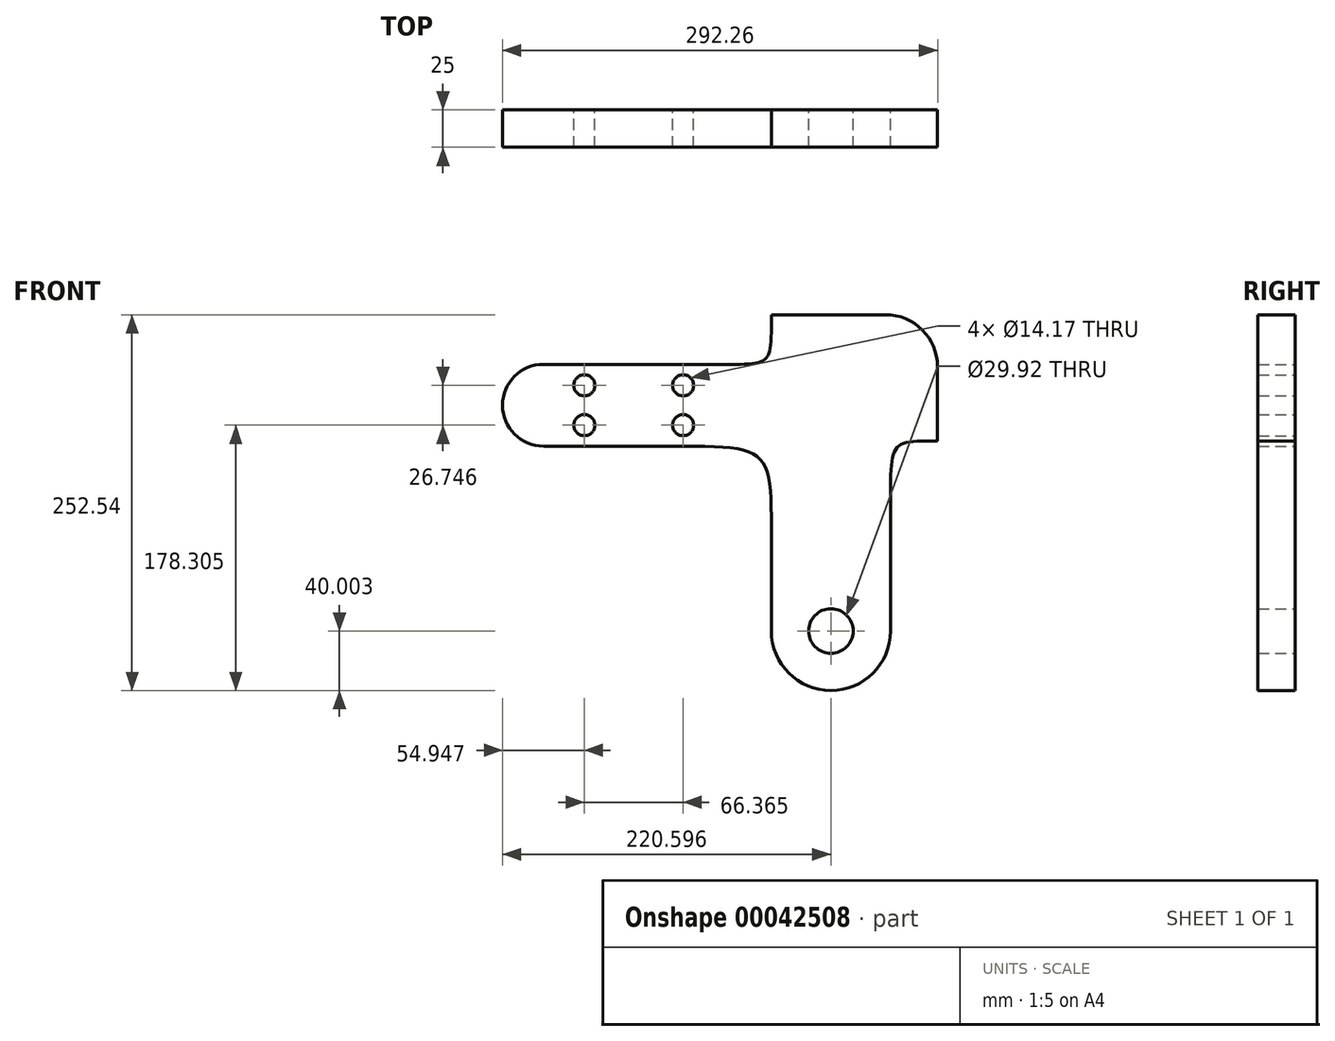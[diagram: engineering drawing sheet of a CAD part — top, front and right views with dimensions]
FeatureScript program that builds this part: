
annotation { "Feature Type Name" : "Feature", "Feature Type Description" : "" }
export const myFeature = defineFeature(function(context is Context, id is Id, definition is map)
    precondition{}
    {
        {
            var Q0;
            Q0=qCreatedBy(makeId("Front.planeOp"),FACE);
            var sketch = newSketch(context, id + "F0", { "sketchPlane" : qUnion([Q0])});
            skLineSegment(sketch, "E0.right", {"start": v(22.5, -51.4) * mm, "end": v(22.5, -113.49) * mm});
            skCircle(sketch, "E1.MirrorC", {"center": v(-36.78, 51.56) * mm, "radius": 7.09 * mm});
            skLineSegment(sketch, "E2.bottom", {"start": v(-9.33, 65.69) * mm, "end": v(-130.6, 65.69) * mm});
            skArc(sketch, "E3", {"start": v(22.5, -113.49) * mm, "mid": v(62.5, -153.49) * mm, "end": v(102.5, -113.49) * mm});
            skFitSpline(sketch, "E4", {"points": [v(22.5, 99.05) * mm, v(-9.33, 65.69) * mm], "startDerivative": vector(0, -103.64) * mm, "endDerivative": vector(-95.5, 0) * mm});
            skFitSpline(sketch, "E5", {"points": [v(134.17, 14.05) * mm, v(102.5, -26.39) * mm], "startDerivative": vector(-94.98, 1.46) * mm, "endDerivative": vector(0, -121.82) * mm});
            skCircle(sketch, "E6", {"center": v(62.5, -113.49) * mm, "radius": 14.96 * mm});
            skLineSegment(sketch, "E7.trimOffspring", {"start": v(22.5, -113.49) * mm, "end": v(22.5, -113.49) * mm});
            skPoint(sketch, "E8.orphan", {"position": v(22.5, 10.69) * mm});
            skLineSegment(sketch, "E9", {"start": v(134.17, 99.05) * mm, "end": v(134.17, 14.05) * mm});
            skLineSegment(sketch, "E10", {"start": v(22.5, 99.05) * mm, "end": v(134.17, 99.05) * mm});
            skLineSegment(sketch, "E0.top", {"start": v(102.5, -113.49) * mm, "end": v(102.5, -113.49) * mm});
            skCircle(sketch, "E11.MirrorC", {"center": v(-36.78, 24.82) * mm, "radius": 7.09 * mm});
            skLineSegment(sketch, "E2.top", {"start": v(-45.4, 10.69) * mm, "end": v(-130.6, 10.69) * mm});
            skArc(sketch, "E12", {"start": v(-130.6, 65.69) * mm, "mid": v(-158.1, 38.19) * mm, "end": v(-130.6, 10.69) * mm});
            skFitSpline(sketch, "E13", {"points": [v(-45.4, 10.69) * mm, v(22.5, -51.4) * mm], "startDerivative": vector(203.7, 0) * mm, "endDerivative": vector(0, -186.26) * mm});
            skLineSegment(sketch, "E14.trimOffspring", {"start": v(102.5, -26.39) * mm, "end": v(102.5, -113.49) * mm});
            skCircle(sketch, "E15", {"center": v(-103.14, 51.56) * mm, "radius": 7.09 * mm});
            skPoint(sketch, "E16.startSnap0", {"position": v(-69.96, 65.69) * mm});
            skCircle(sketch, "E17.MirrorC", {"center": v(-103.14, 24.82) * mm, "radius": 7.09 * mm});
            skLineSegment(sketch, "E18.filletArc", {"start": v(22.5, 10.69) * mm, "end": v(22.5, 10.69) * mm});
            skSolve(sketch);
        }
        {
            var Q0;
            Q0=makeQuery(id+"F0.imprint","IMPRINT",FACE,{"disambiguationData":[TD([[makeQuery(id+"F0.imprint","IMPRINT",EDGE,{"derivedFrom":sQuery(id+"F0.wireOp",EDGE,"E0.right")}),1.0]])]});
            extrude(context, id + "F1", {"entities" : qUnion([Q0]), "depth" : 25 * mm});
        }
        {
            var Q0;
            Q0=makeQuery(id+"F1.opExtrude","SWEPT_EDGE",EDGE,{"disambiguationData":[OSD([sQuery(id+"F0.wireOp",EDGE,"E9"),sQuery(id+"F0.wireOp",EDGE,"E10")])]});
            fillet(context, id + "F2", {"entities" : qUnion([Q0]), "radius" : 35 * mm, "tangentPropagation" : true, "allowEdgeOverflow" : false});
        }
    });
